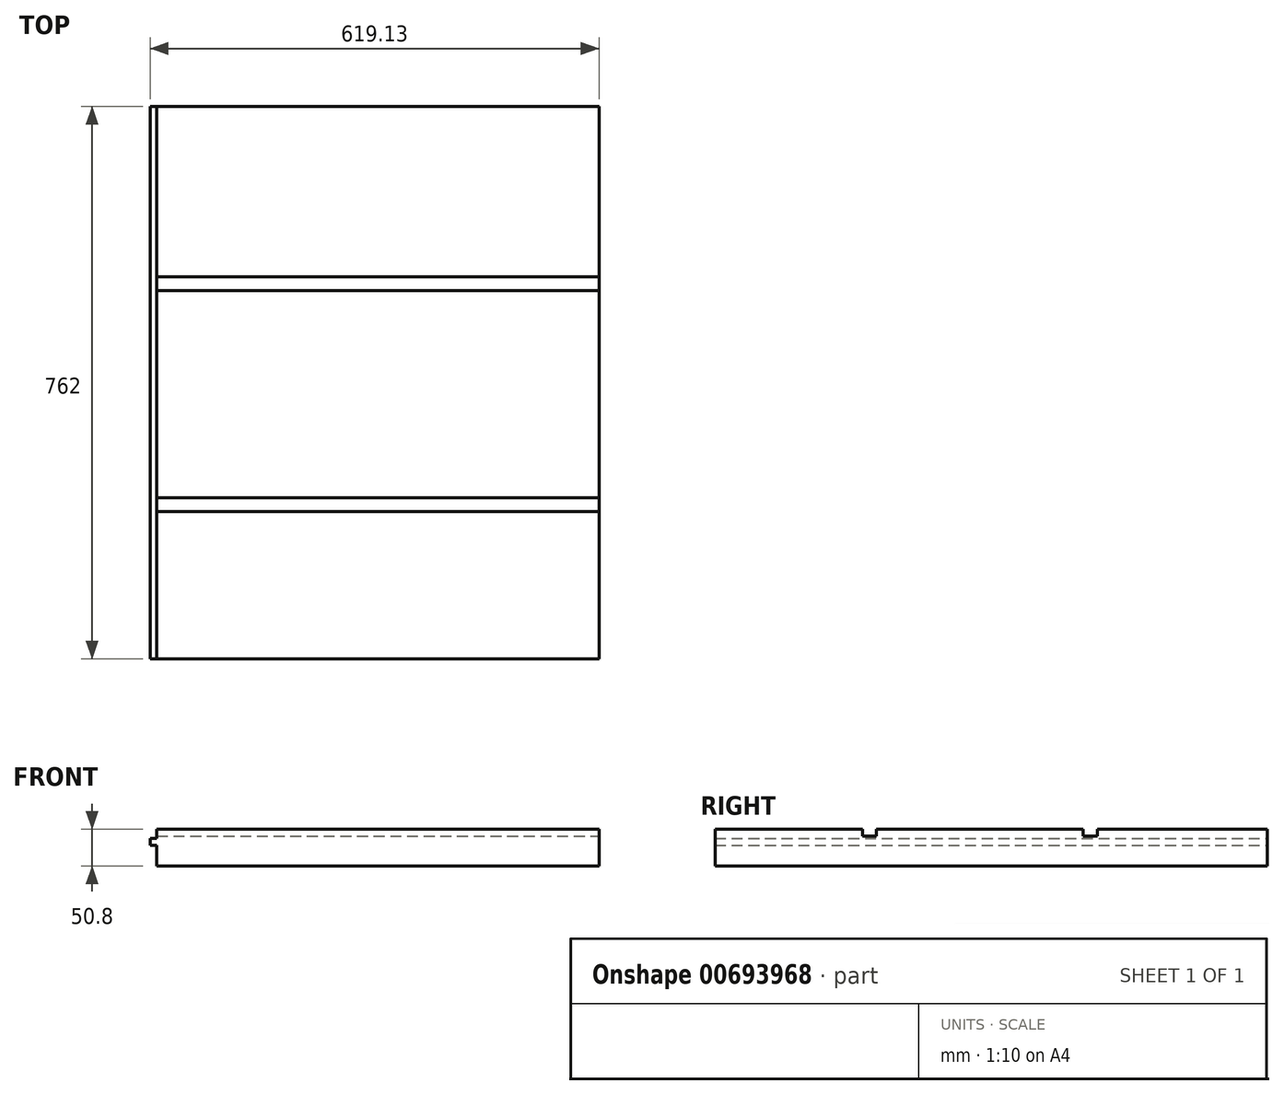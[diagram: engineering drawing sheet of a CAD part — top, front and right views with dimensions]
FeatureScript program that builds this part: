
annotation { "Feature Type Name" : "Feature", "Feature Type Description" : "" }
export const myFeature = defineFeature(function(context is Context, id is Id, definition is map)
    precondition{}
    {
        {
            var Q0;
            Q0=qCreatedBy(makeId("Front.planeOp"),FACE);
            var sketch = newSketch(context, id + "F0", { "sketchPlane" : qUnion([Q0])});
            skLineSegment(sketch, "E0.bottom", {"start": v(0, 0) * mm, "end": v(609.6, 0) * mm});
            skLineSegment(sketch, "E0.top", {"start": v(0, 50.8) * mm, "end": v(609.6, 50.8) * mm});
            skLineSegment(sketch, "E0.left", {"start": v(0, 0) * mm, "end": v(0, 50.8) * mm});
            skLineSegment(sketch, "E0.right", {"start": v(609.6, 0) * mm, "end": v(609.6, 50.8) * mm});
            skLineSegment(sketch, "E1.bottom", {"start": v(-9.53, 38.1) * mm, "end": v(0, 38.1) * mm});
            skLineSegment(sketch, "E1.top", {"start": v(-9.53, 28.58) * mm, "end": v(0, 28.58) * mm});
            skLineSegment(sketch, "E1.left", {"start": v(0, 38.1) * mm, "end": v(0, 28.58) * mm});
            skLineSegment(sketch, "E1.right", {"start": v(-9.53, 38.1) * mm, "end": v(-9.53, 28.58) * mm});
            skSolve(sketch);
        }
        {
            var Q0;
            Q0=makeQuery(id+"F0.imprint","IMPRINT",FACE,{"disambiguationData":[TD([[makeQuery(id+"F0.imprint","IMPRINT",EDGE,{"derivedFrom":sQuery(id+"F0.wireOp",EDGE,"E1.bottom")}),-1.0]])]});
            var Q1;
            {var subQ3=sQuery(id+"F0.wireOp",EDGE,"E0.bottom");Q1=makeQuery(id+"F0.imprint","IMPRINT",FACE,{"disambiguationData":[TD([[makeQuery(id+"F0.imprint","IMPRINT",EDGE,{"derivedFrom":subQ3}),1.0]])]});}
            extrude(context, id + "F1", {"entities" : qUnion([Q0, Q1]), "depth" : 762 * mm, "offsetDistance" : 25.4 * mm});
        }
        {
            var Q0;
            Q0=makeQuery(id+"F1.opExtrude","SWEPT_FACE",FACE,{"disambiguationData":[OSD([sQuery(id+"F0.wireOp",EDGE,"E0.right")])]});
            var sketch = newSketch(context, id + "F2", { "sketchPlane" : qUnion([Q0])});
            skLineSegment(sketch, "E2.bottom", {"start": v(-558.8, 50.8) * mm, "end": v(-539.75, 50.8) * mm});
            skLineSegment(sketch, "E2.top", {"start": v(-558.8, 41.27) * mm, "end": v(-539.75, 41.27) * mm});
            skLineSegment(sketch, "E2.left", {"start": v(-558.8, 50.8) * mm, "end": v(-558.8, 41.27) * mm});
            skLineSegment(sketch, "E2.right", {"start": v(-539.75, 50.8) * mm, "end": v(-539.75, 41.27) * mm});
            skLineSegment(sketch, "E3.1.0.0", {"start": v(-234.95, 50.8) * mm, "end": v(-234.95, 41.27) * mm});
            skLineSegment(sketch, "E3.1.0.1", {"start": v(-254, 50.8) * mm, "end": v(-254, 41.27) * mm});
            skLineSegment(sketch, "E3.1.0.2", {"start": v(-254, 41.27) * mm, "end": v(-234.95, 41.27) * mm});
            skLineSegment(sketch, "E3.1.0.3", {"start": v(-254, 50.8) * mm, "end": v(-234.95, 50.8) * mm});
            skLineSegment(sketch, "E3.direction1", {"start": v(-558.8, 41.27) * mm, "end": v(-254, 41.27) * mm, "construction": true});
            skSolve(sketch);
        }
        {
            var Q0;
            Q0=makeQuery(id+"F2.imprint","IMPRINT",FACE,{"disambiguationData":[TD([[makeQuery(id+"F2.imprint","IMPRINT",EDGE,{"derivedFrom":sQuery(id+"F2.wireOp",EDGE,"E3.1.0.0")}),-1.0]])]});
            var Q1;
            Q1=makeQuery(id+"F2.imprint","IMPRINT",FACE,{"disambiguationData":[TD([[makeQuery(id+"F2.imprint","IMPRINT",EDGE,{"derivedFrom":sQuery(id+"F2.wireOp",EDGE,"E2.bottom")}),-1.0]])]});
            extrude(context, id + "F3", {"entities" : qUnion([Q0, Q1]), "operationType" : NewBodyOperationType.REMOVE, "endBound" : BoundingType.UP_TO_NEXT, "oppositeDirection" : true, "depth" : 25.4 * mm, "offsetDistance" : 25.4 * mm});
        }
    });
